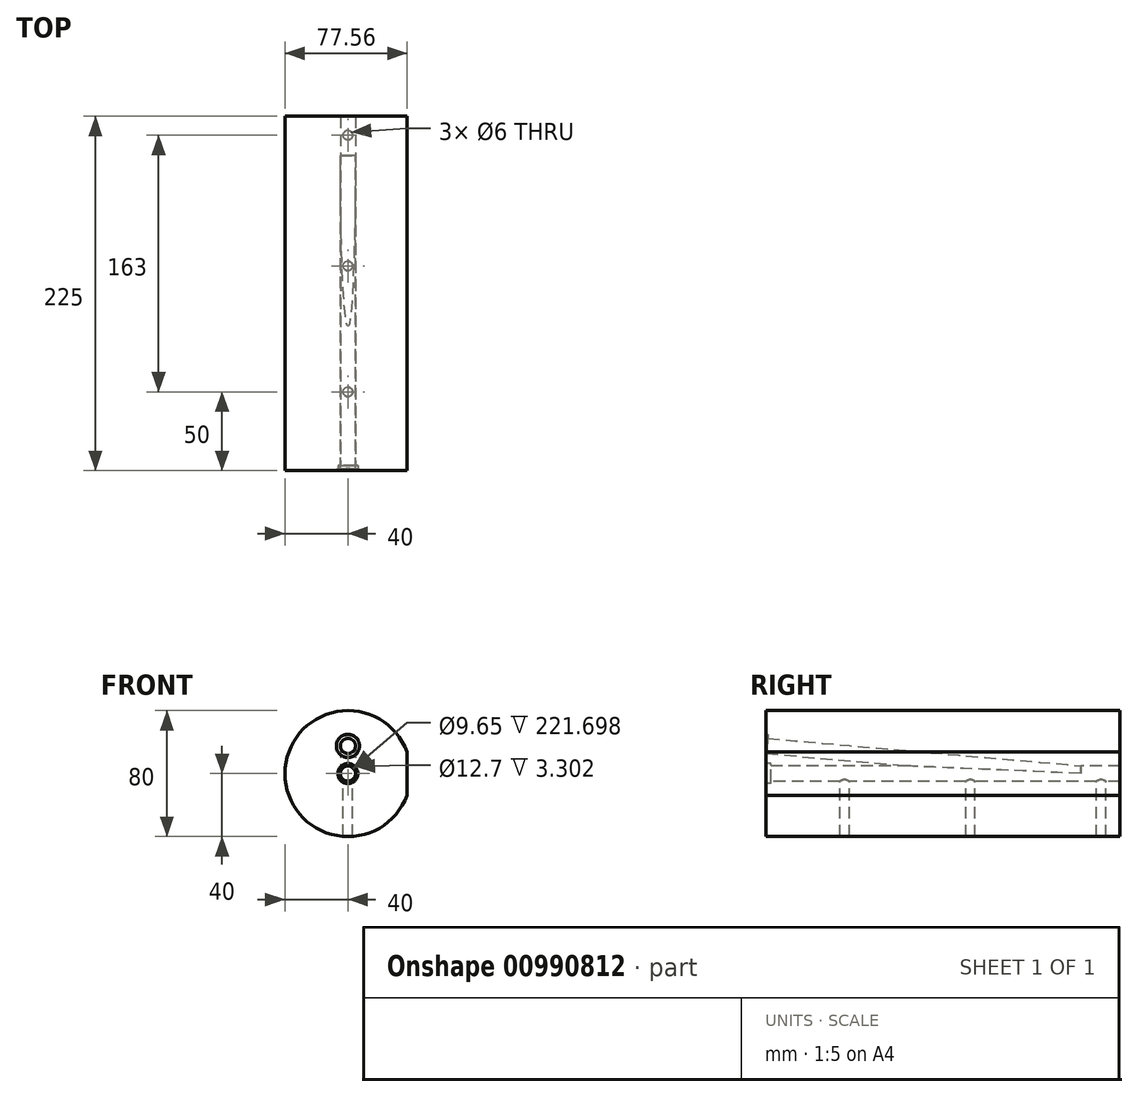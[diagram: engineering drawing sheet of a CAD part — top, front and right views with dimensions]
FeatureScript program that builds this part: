
annotation { "Feature Type Name" : "Feature", "Feature Type Description" : "" }
export const myFeature = defineFeature(function(context is Context, id is Id, definition is map)
    precondition{}
    {
        {
            var Q0;
            Q0=qCreatedBy(makeId("Front.planeOp"),FACE);
            var sketch = newSketch(context, id + "F0", { "sketchPlane" : qUnion([Q0])});
            skCircle(sketch, "E0", {"center": v(0, 0) * mm, "radius": 40 * mm});
            skSolve(sketch);
        }
        {
            var Q0;
            Q0 = qSketchRegion(id + "F0", true);
            extrude(context, id + "F1", {"entities" : qUnion([Q0]), "depth" : 200 * mm, "offsetDistance" : 25 * mm});
        }
        {
            var Q0;
            Q0=makeQuery(id+"F1.opExtrude","CAP_FACE",FACE,{"disambiguationData":[OSD([sQuery(id+"F0.wireOp",EDGE,"E0")])],"isStart":false});
            var sketch = newSketch(context, id + "F2", { "sketchPlane" : qUnion([Q0])});
            skCircle(sketch, "E1", {"center": v(0, 0) * mm, "radius": 4.82 * mm});
            skSolve(sketch);
        }
        {
            var Q0;
            Q0 = qSketchRegion(id + "F2", true);
            extrude(context, id + "F3", {"entities" : qUnion([Q0]), "operationType" : NewBodyOperationType.REMOVE, "endBound" : BoundingType.THROUGH_ALL, "oppositeDirection" : true, "depth" : 400 * mm, "offsetDistance" : 25 * mm});
        }
        {
            var Q0;
            Q0=makeQuery(id+"F1.opExtrude","CAP_FACE",FACE,{"disambiguationData":[OSD([sQuery(id+"F0.wireOp",EDGE,"E0")])],"isStart":false});
            var sketch = newSketch(context, id + "F4", { "sketchPlane" : qUnion([Q0])});
            skCircle(sketch, "E2", {"center": v(0, 0) * mm, "radius": 6.35 * mm});
            skSolve(sketch);
        }
        {
            var Q0;
            Q0 = qSketchRegion(id + "F4", true);
            extrude(context, id + "F5", {"entities" : qUnion([Q0]), "operationType" : NewBodyOperationType.REMOVE, "oppositeDirection" : true, "depth" : (.13 * 25.4) * mm, "offsetDistance" : 25 * mm});
        }
        {
            var Q0;
            Q0=qCreatedBy(makeId("Right.planeOp"),FACE);
            var sketch = newSketch(context, id + "F6", { "sketchPlane" : qUnion([Q0])});
            skPoint(sketch, "E3", {"position": v(-200, 17.63) * mm});
            skLineSegment(sketch, "E4", {"start": v(0, 0) * mm, "end": v(-200, 0) * mm});
            skLineSegment(sketch, "E5", {"start": v(-201.4, 17.75) * mm, "end": v(2.82, -0.12) * mm});
            skLineSegment(sketch, "E6", {"start": v(2.82, -0.12) * mm, "end": v(1.04, -4.8) * mm});
            skLineSegment(sketch, "E7.0", {"start": v(-199.58, 12.75) * mm, "end": v(-199.8, 10.23) * mm});
            skLineSegment(sketch, "E8", {"start": v(-199.8, 10.23) * mm, "end": v(-202.36, 10.45) * mm});
            skLineSegment(sketch, "E9", {"start": v(-202.36, 10.45) * mm, "end": v(-201.4, 17.75) * mm});
            skLineSegment(sketch, "E10.trimOffspring", {"start": v(-199.58, 12.75) * mm, "end": v(1.04, -4.8) * mm});
            skSolve(sketch);
        }
        {
            var Q0;
            Q0 = qSketchRegion(id + "F6", true);
            var Q1;
            Q1=sQuery(id+"F6.wireOp",EDGE,"E5");
            revolve(context, id + "F7", {"operationType" : NewBodyOperationType.REMOVE, "surfaceOperationType" : NewSurfaceOperationType.NEW, "entities" : qUnion([Q0]), "axis" : qUnion([Q1]), "revolveType" : RevolveType.FULL, "oppositeDirection" : true});
        }
        {
            var Q0;
            Q0=makeQuery(id+"F1.opExtrude","CAP_FACE",FACE,{"disambiguationData":[OSD([sQuery(id+"F0.wireOp",EDGE,"E0")])],"isStart":true});
            var sketch = newSketch(context, id + "F8", { "sketchPlane" : qUnion([Q0])});
            skCircle(sketch, "E11", {"center": v(0, 0) * mm, "radius": 40 * mm});
            skSolve(sketch);
        }
        {
            var Q0;
            Q0 = qSketchRegion(id + "F8", true);
            extrude(context, id + "F9", {"entities" : qUnion([Q0]), "operationType" : NewBodyOperationType.ADD, "depth" : 25 * mm, "offsetDistance" : 25 * mm});
        }
        {
            var Q0;
            Q0=makeQuery(id+"F9.opExtrude","CAP_FACE",FACE,{"disambiguationData":[OSD([sQuery(id+"F8.wireOp",EDGE,"E11")])],"isStart":false});
            var sketch = newSketch(context, id + "F10", { "sketchPlane" : qUnion([Q0])});
            skCircle(sketch, "E12", {"center": v(0, 0) * mm, "radius": 4.83 * mm});
            skSolve(sketch);
        }
        {
            var Q0;
            Q0 = qSketchRegion(id + "F10", true);
            extrude(context, id + "F11", {"entities" : qUnion([Q0]), "operationType" : NewBodyOperationType.REMOVE, "oppositeDirection" : true, "depth" : 25 * mm, "offsetDistance" : 25 * mm});
        }
        {
            var Q0;
            Q0=qCreatedBy(makeId("Top.planeOp"),FACE);
            var sketch = newSketch(context, id + "F12", { "sketchPlane" : qUnion([Q0])});
            skCircle(sketch, "E13", {"center": v(0, -150) * mm, "radius": 3 * mm});
            skCircle(sketch, "E14", {"center": v(0, -70) * mm, "radius": 3 * mm});
            skCircle(sketch, "E15", {"center": v(0, 13) * mm, "radius": 3 * mm});
            skSolve(sketch);
        }
        {
            var Q0;
            Q0 = qSketchRegion(id + "F12", true);
            extrude(context, id + "F13", {"entities" : qUnion([Q0]), "operationType" : NewBodyOperationType.REMOVE, "oppositeDirection" : true, "depth" : 50 * mm, "offsetDistance" : 25 * mm});
        }
        {
            var Q0;
            Q0=qCreatedBy(makeId("Front.planeOp"),FACE);
            var sketch = newSketch(context, id + "F14", { "sketchPlane" : qUnion([Q0])});
            skLineSegment(sketch, "E16", {"start": v(37.56, 34.72) * mm, "end": v(37.56, -44.29) * mm});
            skLineSegment(sketch, "E17", {"start": v(37.56, 34.72) * mm, "end": v(53.15, 6.38) * mm});
            skLineSegment(sketch, "E18", {"start": v(53.15, 6.38) * mm, "end": v(53.15, -19.84) * mm});
            skLineSegment(sketch, "E19", {"start": v(53.15, -19.84) * mm, "end": v(37.56, -44.29) * mm});
            skSolve(sketch);
        }
        {
            var Q0;
            Q0 = qSketchRegion(id + "F14", true);
            extrude(context, id + "F15", {"entities" : qUnion([Q0]), "operationType" : NewBodyOperationType.REMOVE, "endBound" : BoundingType.SYMMETRIC, "oppositeDirection" : true, "depth" : 600 * mm, "offsetDistance" : 25 * mm});
        }
    });
